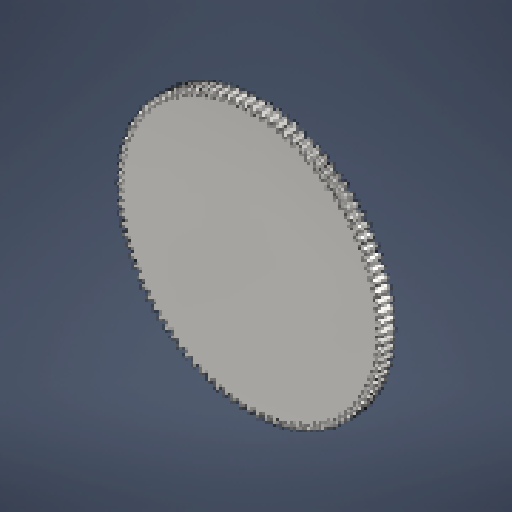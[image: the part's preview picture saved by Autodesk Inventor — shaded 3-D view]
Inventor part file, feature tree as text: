
AUTODESK INVENTOR PART (.ipt)
format: ipt  version: 2024.3 (Build 283343000, 343)  size: 515,584 bytes
history: native  units: mm (DEFAULTED — no unit token found)
features: plane x3, other x3, extrude x1, sketch x1
ambient origin geometry x8: Origin, YZ Plane, XZ Plane, XY Plane, X Axis, Y Axis, Z Axis, Center Point
bodies: Solid1 (feature_tree)
feature tree (8):
  extrude  "Extrusion1"  Depth=12.7mm TaperAngle=0.0deg
  plane  "Work Plane1"
  plane  "Work Plane2"
  plane  "Work Plane3"
  other  "Spur Gear"
  sketch  "Sketch1"  dims[d0=259.08mm d1=12.7mm d2=0.0mm d3=254.0mm d4=76.2mm d5=0.0mm d6=0.0mm d7=0.314159mm d9=0.0mm d14=0.0mm d15=158.75mm d16=0.0mm d17=0.0mm d18=0.0mm d19=158.75mm]
  other  "Srf1"
  other  "Pitch Diameter"
